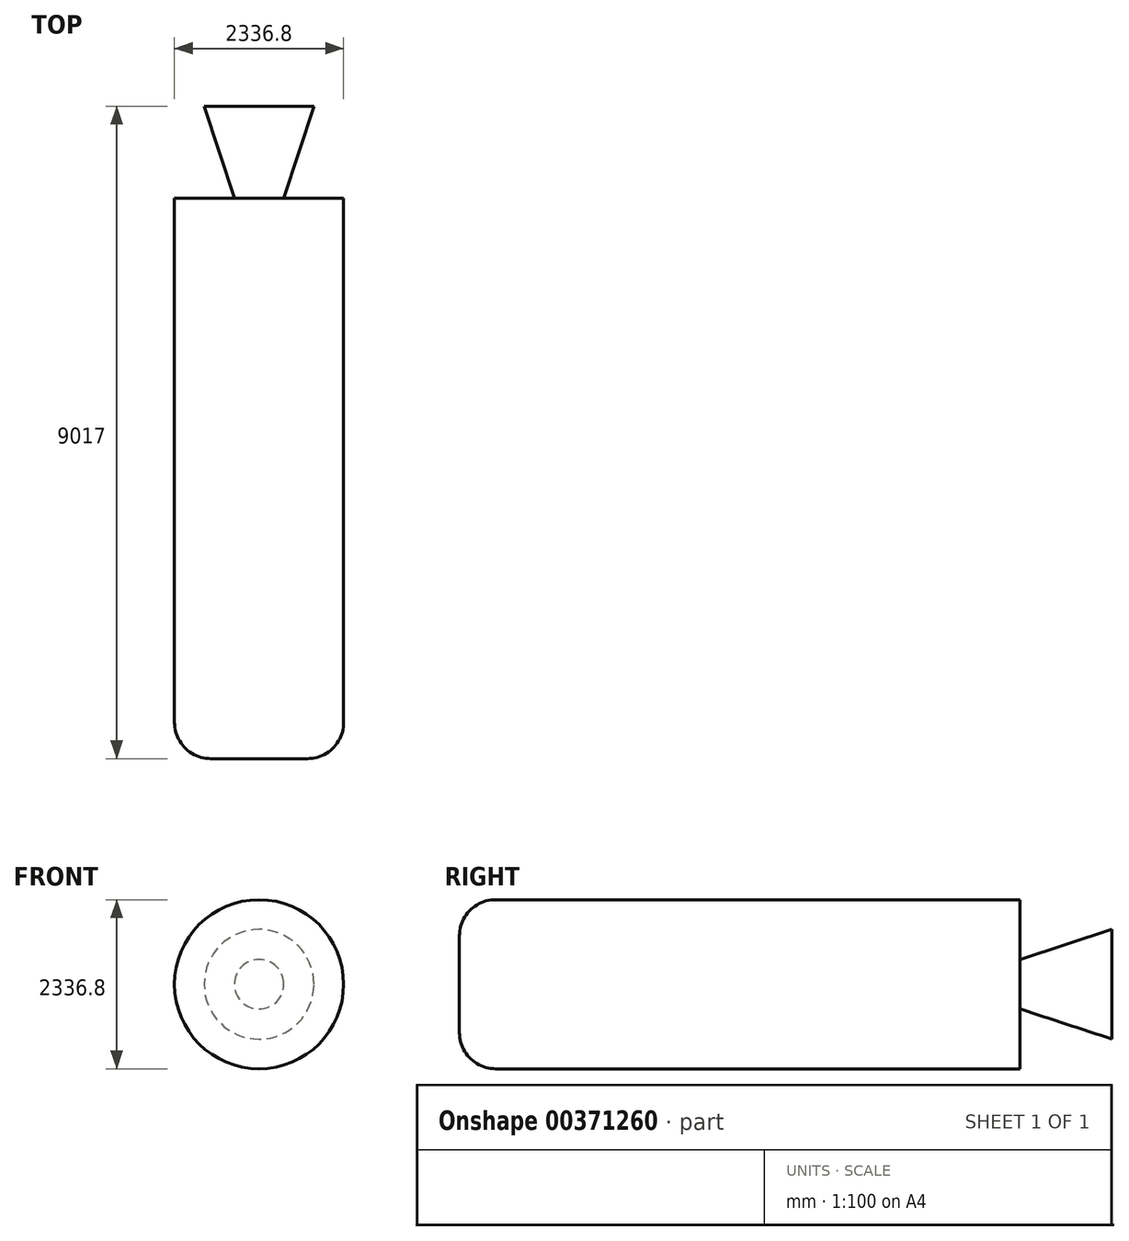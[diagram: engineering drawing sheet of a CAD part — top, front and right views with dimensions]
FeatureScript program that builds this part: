
annotation { "Feature Type Name" : "Feature", "Feature Type Description" : "" }
export const myFeature = defineFeature(function(context is Context, id is Id, definition is map)
    precondition{}
    {
        {
            var Q0;
            Q0=qCreatedBy(makeId("Front.planeOp"),FACE);
            var sketch = newSketch(context, id + "F0", { "sketchPlane" : qUnion([Q0])});
            skCircle(sketch, "E0", {"center": v(0, 0) * mm, "radius": 1168.4 * mm});
            skSolve(sketch);
        }
        {
            var Q0;
            Q0 = qSketchRegion(id + "F0", true);
            extrude(context, id + "F1", {"entities" : qUnion([Q0]), "depth" : 7747 * mm});
        }
        {
            var Q0;
            Q0=qCreatedBy(makeId("Right.planeOp"),FACE);
            var sketch = newSketch(context, id + "F2", { "sketchPlane" : qUnion([Q0])});
            skLineSegment(sketch, "E1", {"start": v(0, 0) * mm, "end": v(1270, 0) * mm});
            skLineSegment(sketch, "E2", {"start": v(1270, 0) * mm, "end": v(1270, 758.19) * mm});
            skLineSegment(sketch, "E3", {"start": v(0, 341.83) * mm, "end": v(1270, 758.19) * mm});
            skLineSegment(sketch, "E4", {"start": v(0, 341.83) * mm, "end": v(0, 0) * mm});
            skSolve(sketch);
        }
        {
            var Q0;
            Q0=makeQuery(id+"F2.imprint","IMPRINT",FACE,{"disambiguationData":[TD([[makeQuery(id+"F2.imprint","IMPRINT",EDGE,{"derivedFrom":sQuery(id+"F2.wireOp",EDGE,"E1")}),1.0]])]});
            var Q1;
            Q1=sQuery(id+"F2.wireOp",EDGE,"E1");
            revolve(context, id + "F3", {"operationType" : NewBodyOperationType.ADD, "entities" : qUnion([Q0]), "axis" : qUnion([Q1]), "revolveType" : RevolveType.FULL});
        }
        {
            var Q0;
            Q0=makeQuery(id+"F1.opExtrude","CAP_EDGE",EDGE,{"disambiguationData":[OSD([sQuery(id+"F0.wireOp",EDGE,"E0")])],"isStart":false});
            fillet(context, id + "F4", {"entities" : qUnion([Q0]), "radius" : 500 * mm, "tangentPropagation" : true, "allowEdgeOverflow" : false});
        }
    });
